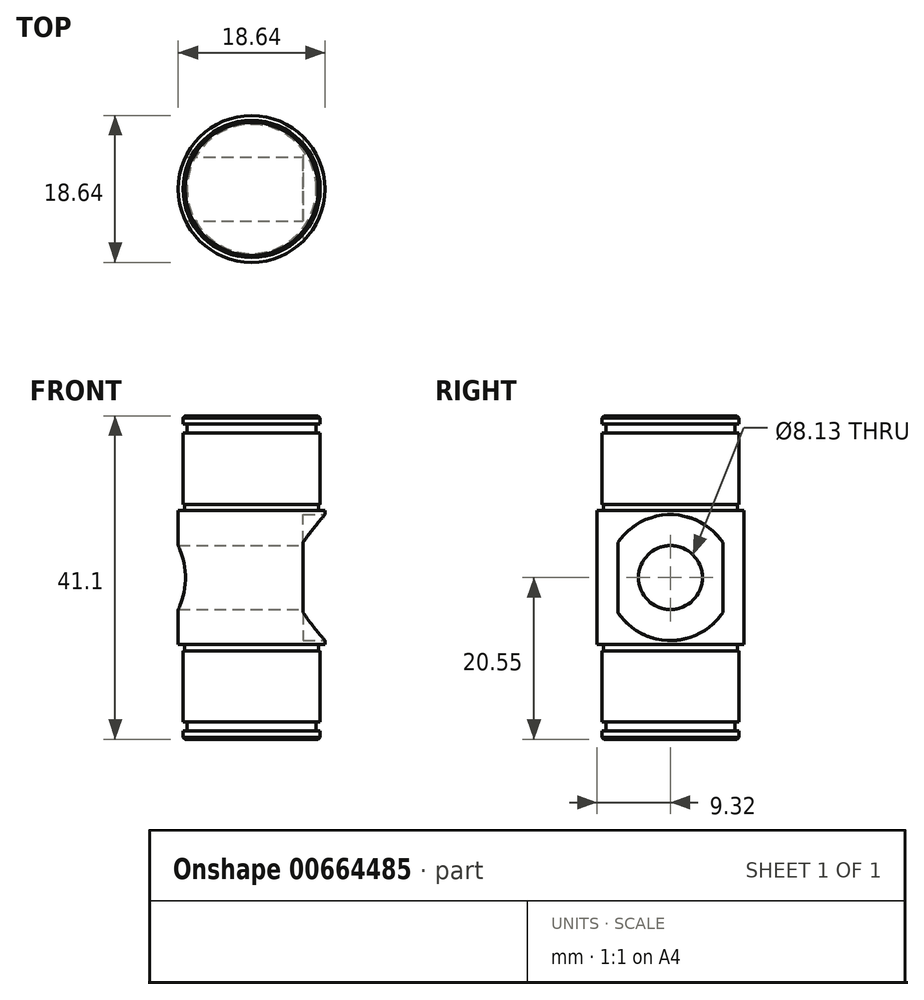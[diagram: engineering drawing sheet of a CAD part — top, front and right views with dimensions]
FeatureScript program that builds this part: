
annotation { "Feature Type Name" : "Feature", "Feature Type Description" : "" }
export const myFeature = defineFeature(function(context is Context, id is Id, definition is map)
    precondition{}
    {
        {
            var Q0;
            Q0=qCreatedBy(makeId("Right.planeOp"),FACE);
            var sketch = newSketch(context, id + "F0", { "sketchPlane" : qUnion([Q0])});
            skLineSegment(sketch, "E0.bottom", {"start": v(0, 0) * mm, "end": v(9.32, 0) * mm});
            skLineSegment(sketch, "E0.top", {"start": v(0, -8.5) * mm, "end": v(9.32, -8.5) * mm});
            skLineSegment(sketch, "E0.left", {"start": v(0, 0) * mm, "end": v(0, -8.5) * mm});
            skLineSegment(sketch, "E0.right", {"start": v(9.32, 0) * mm, "end": v(9.32, -8.5) * mm});
            skLineSegment(sketch, "E1.bottom", {"start": v(0, 0) * mm, "end": v(8.71, 0) * mm});
            skLineSegment(sketch, "E1.top", {"start": v(0, -20.55) * mm, "end": v(8.71, -20.55) * mm});
            skLineSegment(sketch, "E1.left", {"start": v(0, 0) * mm, "end": v(0, -20.55) * mm});
            skLineSegment(sketch, "E1.right", {"start": v(8.71, 0) * mm, "end": v(8.71, -20.55) * mm});
            skLineSegment(sketch, "E2.MirrorCS", {"start": v(9.32, 0) * mm, "end": v(9.32, 8.5) * mm});
            skLineSegment(sketch, "E3.MirrorCS", {"start": v(8.71, 0) * mm, "end": v(8.71, 20.55) * mm});
            skLineSegment(sketch, "E4.MirrorCS", {"start": v(0, 0) * mm, "end": v(0, 20.55) * mm});
            skLineSegment(sketch, "E5.MirrorCS", {"start": v(0, 8.5) * mm, "end": v(9.32, 8.5) * mm});
            skLineSegment(sketch, "E6.MirrorCS", {"start": v(0, 20.55) * mm, "end": v(8.71, 20.55) * mm});
            skSolve(sketch);
        }
        {
            var Q0;
            Q0 = qSketchRegion(id + "F0", true);
            var Q1;
            Q1=sQuery(id+"F0.wireOp",EDGE,"E4.MirrorCS");
            revolve(context, id + "F1", {"entities" : qUnion([Q0]), "axis" : qUnion([Q1]), "revolveType" : RevolveType.FULL});
        }
        {
            var Q0;
            Q0=qCreatedBy(makeId("Right.planeOp"),FACE);
            var sketch = newSketch(context, id + "F2", { "sketchPlane" : qUnion([Q0])});
            skCircle(sketch, "E7", {"center": v(0, 0) * mm, "radius": 4.06 * mm});
            skSolve(sketch);
        }
        {
            var Q0;
            Q0 = qSketchRegion(id + "F2", true);
            extrude(context, id + "F3", {"entities" : qUnion([Q0]), "operationType" : NewBodyOperationType.REMOVE, "endBound" : BoundingType.THROUGH_ALL, "oppositeDirection" : true, "depth" : 25.4 * mm, "offsetDistance" : 25.4 * mm, "hasSecondDirection" : true, "secondDirectionBound" : SecondDirectionBoundingType.THROUGH_ALL, "secondDirectionOppositeDirection" : false, "secondDirectionDepth" : 25.4 * mm});
        }
        {
            var Q0;
            Q0=qCreatedBy(makeId("Front.planeOp"),FACE);
            var sketch = newSketch(context, id + "F4", { "sketchPlane" : qUnion([Q0])});
            skLineSegment(sketch, "E8.bottom", {"start": v(6.53, 0) * mm, "end": v(19.23, 0) * mm});
            skLineSegment(sketch, "E8.top", {"start": v(6.53, -8) * mm, "end": v(19.23, -8) * mm});
            skLineSegment(sketch, "E8.left", {"start": v(6.53, 0) * mm, "end": v(6.53, -8) * mm});
            skLineSegment(sketch, "E8.right", {"start": v(19.23, 0) * mm, "end": v(19.23, -8) * mm});
            skLineSegment(sketch, "E9", {"start": v(9.32, 8.5) * mm, "end": v(9.32, -8.5) * mm});
            skLineSegment(sketch, "E10.MirrorCS", {"start": v(6.53, 0) * mm, "end": v(-6.17, 0) * mm});
            skLineSegment(sketch, "E11.MirrorCS", {"start": v(-6.17, 0) * mm, "end": v(-6.17, -8) * mm});
            skLineSegment(sketch, "E12.MirrorCS", {"start": v(6.53, 0) * mm, "end": v(6.53, 8) * mm});
            skLineSegment(sketch, "E13.MirrorCS", {"start": v(6.53, 8) * mm, "end": v(19.23, 8) * mm});
            skLineSegment(sketch, "E14.MirrorCS", {"start": v(19.23, 0) * mm, "end": v(19.23, 8) * mm});
            skSolve(sketch);
        }
        {
            var Q0;
            {var subQ0=sQuery(id+"F4.wireOp",EDGE,"E8.left");Q0=makeQuery(id+"F4.imprint","IMPRINT",FACE,{"disambiguationData":[TD([[makeQuery(id+"F4.imprint","IMPRINT",EDGE,{"derivedFrom":subQ0}),1.0]])]});}
            var Q1;
            Q1=sQuery(id+"F4.wireOp",EDGE,"E8.bottom");
            revolve(context, id + "F5", {"operationType" : NewBodyOperationType.REMOVE, "entities" : qUnion([Q0]), "axis" : qUnion([Q1]), "revolveType" : RevolveType.FULL, "oppositeDirection" : true});
        }
        {
            var Q0;
            Q0=qCreatedBy(makeId("Right.planeOp"),FACE);
            var sketch = newSketch(context, id + "F6", { "sketchPlane" : qUnion([Q0])});
            skLineSegment(sketch, "E15.0", {"start": v(9.32, -8.5) * mm, "end": v(-9.32, -8.5) * mm});
            skLineSegment(sketch, "E16.bottom", {"start": v(8.5, -8.5) * mm, "end": v(14.86, -8.5) * mm});
            skLineSegment(sketch, "E16.top", {"start": v(8.5, -9.3) * mm, "end": v(14.86, -9.3) * mm});
            skLineSegment(sketch, "E16.left", {"start": v(8.5, -8.5) * mm, "end": v(8.5, -9.3) * mm});
            skLineSegment(sketch, "E16.right", {"start": v(14.86, -8.5) * mm, "end": v(14.86, -9.3) * mm});
            skLineSegment(sketch, "E17", {"start": v(0, 0) * mm, "end": v(0, -20.5) * mm, "construction": true});
            skLineSegment(sketch, "E18", {"start": v(8.71, -8.5) * mm, "end": v(8.71, -20.55) * mm});
            skLineSegment(sketch, "E19", {"start": v(-0.31, 0) * mm, "end": v(25.09, 0) * mm, "construction": true});
            skLineSegment(sketch, "E20.MirrorCS", {"start": v(8.5, 8.5) * mm, "end": v(14.86, 8.5) * mm});
            skLineSegment(sketch, "E21.MirrorCS", {"start": v(14.86, 8.5) * mm, "end": v(14.86, 9.3) * mm});
            skLineSegment(sketch, "E22.MirrorCS", {"start": v(8.5, 9.3) * mm, "end": v(14.86, 9.3) * mm});
            skLineSegment(sketch, "E23.MirrorCS", {"start": v(8.71, 8.5) * mm, "end": v(8.71, 20.55) * mm});
            skLineSegment(sketch, "E24.MirrorCS", {"start": v(8.5, 8.5) * mm, "end": v(8.5, 9.3) * mm});
            skSolve(sketch);
        }
        {
            var Q0;
            Q0 = qSketchRegion(id + "F6", true);
            var Q1;
            Q1=sQuery(id+"F6.wireOp",EDGE,"E17");
            revolve(context, id + "F7", {"operationType" : NewBodyOperationType.REMOVE, "entities" : qUnion([Q0]), "axis" : qUnion([Q1]), "revolveType" : RevolveType.FULL, "oppositeDirection" : true});
        }
        {
            var Q0;
            Q0=qCreatedBy(makeId("Right.planeOp"),FACE);
            var sketch = newSketch(context, id + "F8", { "sketchPlane" : qUnion([Q0])});
            skLineSegment(sketch, "E25", {"start": v(0, 0) * mm, "end": v(17.96, 0) * mm, "construction": true});
            skLineSegment(sketch, "E26", {"start": v(0, 0) * mm, "end": v(0, -20.55) * mm});
            skLineSegment(sketch, "E27", {"start": v(8.71, -9.3) * mm, "end": v(8.71, -20.55) * mm});
            skLineSegment(sketch, "E28.bottom", {"start": v(8.71, -18.34) * mm, "end": v(8.2, -18.34) * mm});
            skLineSegment(sketch, "E28.top", {"start": v(8.71, -19.5) * mm, "end": v(8.2, -19.5) * mm});
            skLineSegment(sketch, "E28.left", {"start": v(8.71, -18.34) * mm, "end": v(8.71, -19.5) * mm});
            skLineSegment(sketch, "E28.right", {"start": v(8.2, -18.34) * mm, "end": v(8.2, -19.5) * mm});
            skLineSegment(sketch, "E29.MirrorCS", {"start": v(8.2, 18.34) * mm, "end": v(8.2, 19.5) * mm});
            skLineSegment(sketch, "E30.MirrorCS", {"start": v(8.71, 18.34) * mm, "end": v(8.2, 18.34) * mm});
            skLineSegment(sketch, "E31.MirrorCS", {"start": v(8.71, 19.5) * mm, "end": v(8.2, 19.5) * mm});
            skLineSegment(sketch, "E32.MirrorCS", {"start": v(8.71, 9.3) * mm, "end": v(8.71, 20.55) * mm});
            skSolve(sketch);
        }
        {
            var Q0;
            Q0 = qSketchRegion(id + "F8", true);
            var Q1;
            Q1=sQuery(id+"F8.wireOp",EDGE,"E26");
            revolve(context, id + "F9", {"operationType" : NewBodyOperationType.REMOVE, "entities" : qUnion([Q0]), "axis" : qUnion([Q1]), "revolveType" : RevolveType.FULL, "oppositeDirection" : true});
        }
        {
            var Q0;
            Q0=makeQuery(id+"F7.boolean.opBoolean","COPY",EDGE,{"derivedFrom":makeQuery(id+"F7.opRevolve","SWEPT_EDGE",EDGE,{"disambiguationData":[OSD([sQuery(id+"F6.wireOp",EDGE,"E16.bottom"),sQuery(id+"F6.wireOp",EDGE,"E16.left")])]})});
            var Q1;
            Q1=makeQuery(id+"F7.boolean.opBoolean","COPY",EDGE,{"derivedFrom":makeQuery(id+"F7.opRevolve","SWEPT_EDGE",EDGE,{"disambiguationData":[OSD([sQuery(id+"F6.wireOp",EDGE,"E16.top"),sQuery(id+"F6.wireOp",EDGE,"E16.left")])]})});
            var Q2;
            Q2=makeQuery(id+"F7.boolean.opBoolean","COPY",EDGE,{"derivedFrom":makeQuery(id+"F7.opRevolve","SWEPT_EDGE",EDGE,{"disambiguationData":[OSD([sQuery(id+"F6.wireOp",EDGE,"E20.MirrorCS"),sQuery(id+"F6.wireOp",EDGE,"E24.MirrorCS")])]})});
            var Q3;
            Q3=makeQuery(id+"F7.boolean.opBoolean","COPY",EDGE,{"derivedFrom":makeQuery(id+"F7.opRevolve","SWEPT_EDGE",EDGE,{"disambiguationData":[OSD([sQuery(id+"F6.wireOp",EDGE,"E22.MirrorCS"),sQuery(id+"F6.wireOp",EDGE,"E24.MirrorCS")])]})});
            fillet(context, id + "F10", {"entities" : qUnion([Q0, Q1, Q2, Q3]), "radius" : 0.13 * mm, "tangentPropagation" : true, "allowEdgeOverflow" : false});
        }
        {
            var Q0;
            Q0=makeQuery(id+"F1.opRevolve","SWEPT_EDGE",EDGE,{"disambiguationData":[OSD([sQuery(id+"F0.wireOp",EDGE,"E3.MirrorCS"),sQuery(id+"F0.wireOp",EDGE,"E6.MirrorCS")])]});
            var Q1;
            Q1=makeQuery(id+"F1.opRevolve","SWEPT_EDGE",EDGE,{"disambiguationData":[OSD([sQuery(id+"F0.wireOp",EDGE,"E1.top"),sQuery(id+"F0.wireOp",EDGE,"E1.right")])]});
            chamfer(context, id + "F11", {"entities" : qUnion([Q0, Q1]), "width" : 0.25 * mm, "tangentPropagation" : true});
        }
    });
